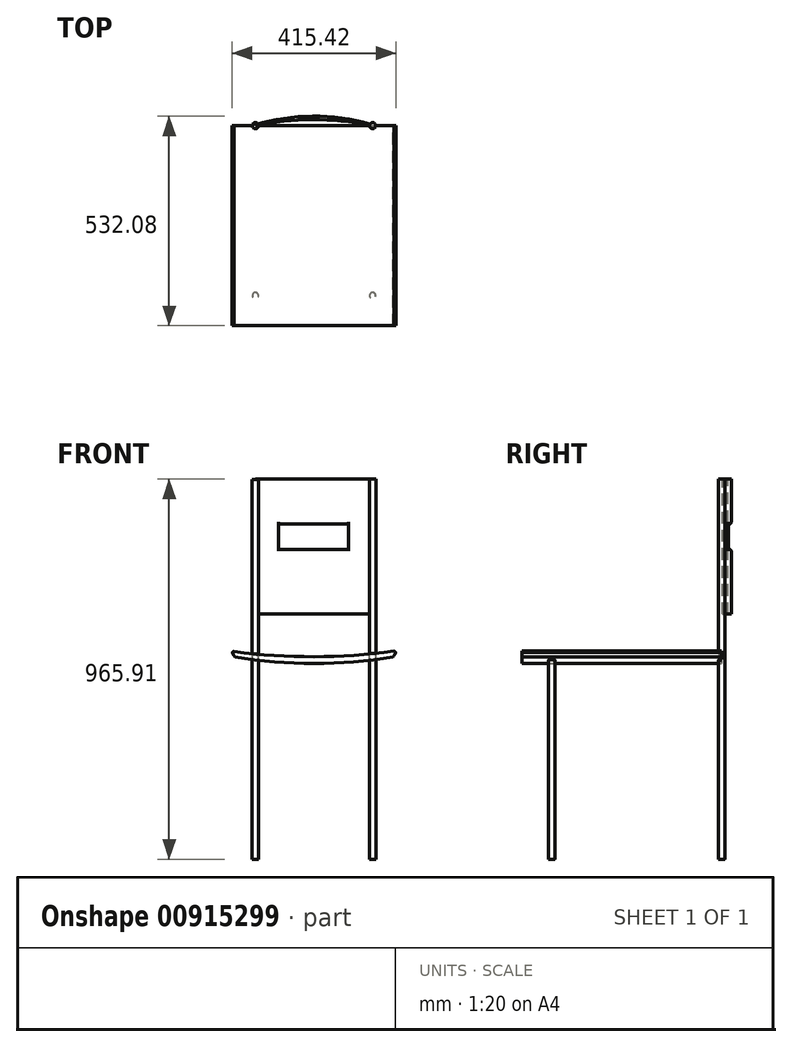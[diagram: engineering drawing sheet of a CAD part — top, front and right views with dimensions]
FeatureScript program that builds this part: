
annotation { "Feature Type Name" : "Feature", "Feature Type Description" : "" }
export const myFeature = defineFeature(function(context is Context, id is Id, definition is map)
    precondition{}
    {
        {
            var Q0;
            Q0=qCreatedBy(makeId("Front.planeOp"),FACE);
            var sketch = newSketch(context, id + "F0", { "sketchPlane" : qUnion([Q0])});
            skArc(sketch, "E0", {"start": v(-203.45, 18.1) * mm, "mid": v(-0.2, 5.21) * mm, "end": v(202.95, 19.47) * mm});
            skArc(sketch, "E1", {"start": v(-203.45, 18.1) * mm, "mid": v(-206.06, 17.6) * mm, "end": v(-207.7, 15.52) * mm});
            skLineSegment(sketch, "E2", {"start": v(-207.7, 15.52) * mm, "end": v(-207.17, 15.52) * mm});
            skArc(sketch, "E3", {"start": v(-207.17, 15.52) * mm, "mid": v(-204.63, 10.07) * mm, "end": v(-201.09, 5.21) * mm});
            skArc(sketch, "E4.MirrorCS", {"start": v(207.17, 15.52) * mm, "mid": v(204.63, 10.07) * mm, "end": v(201.09, 5.21) * mm});
            skLineSegment(sketch, "E5.MirrorCS", {"start": v(207.7, 15.52) * mm, "end": v(207.17, 15.52) * mm});
            skArc(sketch, "E6", {"start": v(207.7, 15.52) * mm, "mid": v(205.84, 18.1) * mm, "end": v(202.95, 19.47) * mm});
            skArc(sketch, "E7", {"start": v(-201.09, 5.21) * mm, "mid": v(0, -12.16) * mm, "end": v(201.09, 5.21) * mm});
            skArc(sketch, "E8", {"start": v(-207.17, 15.52) * mm, "mid": v(0, -0.55) * mm, "end": v(207.17, 15.52) * mm});
            skSolve(sketch);
        }
        {
            var Q0;
            Q0=makeQuery(id+"F0.imprint","IMPRINT",FACE,{"disambiguationData":[TD([[makeQuery(id+"F0.imprint","IMPRINT",EDGE,{"derivedFrom":sQuery(id+"F0.wireOp",EDGE,"E3")}),1.0]])]});
            var Q1;
            Q1=makeQuery(id+"F0.imprint","IMPRINT",FACE,{"disambiguationData":[TD([[makeQuery(id+"F0.imprint","IMPRINT",EDGE,{"derivedFrom":sQuery(id+"F0.wireOp",EDGE,"E0")}),-1.0]])]});
            extrude(context, id + "F1", {"entities" : qUnion([Q0, Q1]), "endBound" : BoundingType.SYMMETRIC, "depth" : 508 * mm, "offsetDistance" : 25.4 * mm});
        }
        {
            var Q0;
            Q0=makeQuery(id+"F1.opExtrude","CAP_FACE",FACE,{"disambiguationData":[OSD([sQuery(id+"F0.wireOp",EDGE,"E0"),sQuery(id+"F0.wireOp",EDGE,"E1"),sQuery(id+"F0.wireOp",EDGE,"E2"),sQuery(id+"F0.wireOp",EDGE,"E3"),sQuery(id+"F0.wireOp",EDGE,"E4.MirrorCS"),sQuery(id+"F0.wireOp",EDGE,"E5.MirrorCS"),sQuery(id+"F0.wireOp",EDGE,"E6"),sQuery(id+"F0.wireOp",EDGE,"E7")])],"isStart":true});
            var sketch = newSketch(context, id + "F2", { "sketchPlane" : qUnion([Q0])});
            skLineSegment(sketch, "E9.MirrorCS", {"start": v(156.85, -1.46) * mm, "end": v(156.85, -509.46) * mm});
            skLineSegment(sketch, "E10", {"start": v(-156.85, -0.75) * mm, "end": v(-156.85, -509.46) * mm});
            skLineSegment(sketch, "E11", {"start": v(-149.06, -2.65) * mm, "end": v(-149.06, -509.46) * mm});
            skLineSegment(sketch, "E12.MirrorCS", {"start": v(149.06, -2.65) * mm, "end": v(149.06, -509.46) * mm});
            skLineSegment(sketch, "E13", {"start": v(-156.85, -509.46) * mm, "end": v(-149.06, -509.46) * mm});
            skLineSegment(sketch, "E14.MirrorCS", {"start": v(156.85, -509.46) * mm, "end": v(149.06, -509.46) * mm});
            skLineSegment(sketch, "E15", {"start": v(-156.85, -0.75) * mm, "end": v(-156.85, 456.45) * mm});
            skLineSegment(sketch, "E16", {"start": v(-149.06, -2.65) * mm, "end": v(-149.06, 456.45) * mm});
            skLineSegment(sketch, "E17", {"start": v(149.06, -2.65) * mm, "end": v(149.06, 454.55) * mm});
            skLineSegment(sketch, "E18", {"start": v(156.85, -1.46) * mm, "end": v(156.85, 455.74) * mm});
            skLineSegment(sketch, "E19", {"start": v(-149.06, 456.45) * mm, "end": v(-156.85, 456.45) * mm});
            skLineSegment(sketch, "E20", {"start": v(156.85, 455.74) * mm, "end": v(149.06, 454.55) * mm});
            skSolve(sketch);
        }
        {
            var Q0;
            {var subQ4=sQuery(id+"F2.wireOp",EDGE,"E11");Q0=makeQuery(id+"F2.imprint","IMPRINT",FACE,{"disambiguationData":[TD([[makeQuery(id+"F2.imprint","IMPRINT",EDGE,{"derivedFrom":subQ4}),-1.0]])]});}
            var Q1;
            Q1=sQuery(id+"F2.wireOp",EDGE,"E11");
            revolve(context, id + "F3", {"operationType" : NewBodyOperationType.ADD, "surfaceOperationType" : NewSurfaceOperationType.NEW, "entities" : qUnion([Q0]), "axis" : qUnion([Q1]), "revolveType" : RevolveType.FULL});
        }
        {
            var Q0;
            {var subQ4=sQuery(id+"F2.wireOp",EDGE,"E12.MirrorCS");Q0=makeQuery(id+"F2.imprint","IMPRINT",FACE,{"disambiguationData":[TD([[makeQuery(id+"F2.imprint","IMPRINT",EDGE,{"derivedFrom":subQ4}),1.0]])]});}
            var Q1;
            Q1=sQuery(id+"F2.wireOp",EDGE,"E12.MirrorCS");
            revolve(context, id + "F4", {"operationType" : NewBodyOperationType.ADD, "surfaceOperationType" : NewSurfaceOperationType.NEW, "entities" : qUnion([Q0]), "axis" : qUnion([Q1]), "revolveType" : RevolveType.FULL});
        }
        {
            var Q0;
            Q0=makeQuery(id+"F1.opExtrude","CAP_FACE",FACE,{"disambiguationData":[OSD([sQuery(id+"F0.wireOp",EDGE,"E0"),sQuery(id+"F0.wireOp",EDGE,"E1"),sQuery(id+"F0.wireOp",EDGE,"E2"),sQuery(id+"F0.wireOp",EDGE,"E3"),sQuery(id+"F0.wireOp",EDGE,"E4.MirrorCS"),sQuery(id+"F0.wireOp",EDGE,"E5.MirrorCS"),sQuery(id+"F0.wireOp",EDGE,"E6"),sQuery(id+"F0.wireOp",EDGE,"E7")])],"isStart":false});
            cPlane(context, id + "F5", {"entities" : qUnion([Q0]), "cplaneType" : CPlaneType.OFFSET, "offset" : 76.2 * mm, "oppositeDirection" : true, "width" : 152.4 * mm, "height" : 152.4 * mm});
        }
        {
            var Q0;
            Q0=qCreatedBy(id+"F5.planeOp",FACE);
            var sketch = newSketch(context, id + "F6", { "sketchPlane" : qUnion([Q0])});
            skLineSegment(sketch, "E21.0", {"start": v(-149.06, -2.65) * mm, "end": v(-149.06, -509.46) * mm});
            skLineSegment(sketch, "E22.0", {"start": v(-156.85, -1.46) * mm, "end": v(-156.85, -509.46) * mm});
            skLineSegment(sketch, "E23.0", {"start": v(149.06, -2.65) * mm, "end": v(149.06, -509.46) * mm});
            skLineSegment(sketch, "E24", {"start": v(156.85, -1.62) * mm, "end": v(156.85, -509.46) * mm});
            skLineSegment(sketch, "E25.0", {"start": v(156.85, -509.46) * mm, "end": v(149.06, -509.46) * mm});
            skLineSegment(sketch, "E26.0", {"start": v(-156.85, -509.46) * mm, "end": v(-149.06, -509.46) * mm});
            skLineSegment(sketch, "E27", {"start": v(-156.85, -1.46) * mm, "end": v(-149.06, -2.65) * mm});
            skLineSegment(sketch, "E28", {"start": v(149.06, -2.65) * mm, "end": v(156.85, -1.62) * mm});
            skSolve(sketch);
        }
        {
            var Q0;
            Q0=makeQuery(id+"F6.imprint","IMPRINT",FACE,{"disambiguationData":[TD([[makeQuery(id+"F6.imprint","IMPRINT",EDGE,{"derivedFrom":sQuery(id+"F6.wireOp",EDGE,"E21.0")}),-1.0]])]});
            var Q1;
            Q1=sQuery(id+"F6.wireOp",EDGE,"E21.0");
            revolve(context, id + "F7", {"operationType" : NewBodyOperationType.ADD, "surfaceOperationType" : NewSurfaceOperationType.NEW, "entities" : qUnion([Q0]), "axis" : qUnion([Q1]), "revolveType" : RevolveType.FULL});
        }
        {
            var Q0;
            Q0=makeQuery(id+"F6.imprint","IMPRINT",FACE,{"disambiguationData":[TD([[makeQuery(id+"F6.imprint","IMPRINT",EDGE,{"derivedFrom":sQuery(id+"F6.wireOp",EDGE,"E23.0")}),1.0]])]});
            var Q1;
            Q1=sQuery(id+"F6.wireOp",EDGE,"E23.0");
            revolve(context, id + "F8", {"operationType" : NewBodyOperationType.ADD, "surfaceOperationType" : NewSurfaceOperationType.NEW, "entities" : qUnion([Q0]), "axis" : qUnion([Q1]), "revolveType" : RevolveType.FULL});
        }
        {
            var Q0;
            {var subQ1=sQuery(id+"F2.wireOp",EDGE,"E16");Q0=makeQuery(id+"F2.imprint","IMPRINT",FACE,{"disambiguationData":[TD([[makeQuery(id+"F2.imprint","IMPRINT",EDGE,{"derivedFrom":subQ1}),1.0]])]});}
            var Q1;
            Q1=sQuery(id+"F2.wireOp",EDGE,"E16");
            revolve(context, id + "F9", {"operationType" : NewBodyOperationType.ADD, "surfaceOperationType" : NewSurfaceOperationType.NEW, "entities" : qUnion([Q0]), "axis" : qUnion([Q1]), "revolveType" : RevolveType.FULL});
        }
        {
            var Q0;
            {var subQ1=sQuery(id+"F2.wireOp",EDGE,"E17");Q0=makeQuery(id+"F2.imprint","IMPRINT",FACE,{"disambiguationData":[TD([[makeQuery(id+"F2.imprint","IMPRINT",EDGE,{"derivedFrom":subQ1}),-1.0]])]});}
            var Q1;
            Q1=sQuery(id+"F2.wireOp",EDGE,"E17");
            revolve(context, id + "F10", {"operationType" : NewBodyOperationType.ADD, "surfaceOperationType" : NewSurfaceOperationType.NEW, "entities" : qUnion([Q0]), "axis" : qUnion([Q1]), "revolveType" : RevolveType.FULL});
        }
        {
            var Q0;
            {var subQ3=sQuery(id+"F2.wireOp",EDGE,"E10");var subQ5=sQuery(id+"F2.wireOp",EDGE,"E15");var subQ6=makeQuery(id+"F2.imprint","INTERSECT",VERTEX,{"derivedFrom":[subQ3,subQ5]});Q0=makeQuery(id+"F2.imprint","IMPRINT",FACE,{"disambiguationData":[TD([[makeQuery(id+"F2.imprint","IMPRINT",EDGE,{"disambiguationData":[TD([[subQ6,-1.0]])],"derivedFrom":subQ3}),1.0]])]});}
            var Q1;
            Q1=sQuery(id+"F2.wireOp",EDGE,"E16");
            revolve(context, id + "F11", {"operationType" : NewBodyOperationType.ADD, "surfaceOperationType" : NewSurfaceOperationType.NEW, "entities" : qUnion([Q0]), "axis" : qUnion([Q1]), "revolveType" : RevolveType.ONE_DIRECTION, "angle" : 180 * degree});
        }
        {
            var Q0;
            {var subQ3=sQuery(id+"F2.wireOp",EDGE,"E9.MirrorCS");var subQ5=sQuery(id+"F2.wireOp",EDGE,"E18");var subQ6=makeQuery(id+"F2.imprint","INTERSECT",VERTEX,{"derivedFrom":[subQ3,subQ5]});Q0=makeQuery(id+"F2.imprint","IMPRINT",FACE,{"disambiguationData":[TD([[makeQuery(id+"F2.imprint","IMPRINT",EDGE,{"disambiguationData":[TD([[subQ6,-1.0]])],"derivedFrom":subQ3}),-1.0]])]});}
            var Q1;
            Q1=sQuery(id+"F2.wireOp",EDGE,"E17");
            revolve(context, id + "F12", {"operationType" : NewBodyOperationType.ADD, "surfaceOperationType" : NewSurfaceOperationType.NEW, "entities" : qUnion([Q0]), "axis" : qUnion([Q1]), "revolveType" : RevolveType.ONE_DIRECTION, "angle" : 0 * degree});
        }
        {
            var Q0;
            Q0=makeQuery(id+"F9.opRevolve","SWEPT_FACE",FACE,{"disambiguationData":[OSD([sQuery(id+"F2.wireOp",EDGE,"E19")])]});
            var sketch = newSketch(context, id + "F13", { "sketchPlane" : qUnion([Q0])});
            skArc(sketch, "E29", {"start": v(149.06, 254) * mm, "mid": v(0, 269.39) * mm, "end": v(-149.06, 254) * mm});
            skLineSegment(sketch, "E30", {"start": v(-149.06, 254) * mm, "end": v(-149.06, 256.54) * mm});
            skLineSegment(sketch, "E31", {"start": v(149.06, 254) * mm, "end": v(149.06, 256.54) * mm});
            skArc(sketch, "E32", {"start": v(149.06, 256.54) * mm, "mid": v(0, 278.08) * mm, "end": v(-149.06, 256.54) * mm});
            skSolve(sketch);
        }
        {
            var Q0;
            {var subQ0=sQuery(id+"F13.wireOp",EDGE,"E30");Q0=makeQuery(id+"F13.imprint","IMPRINT",FACE,{"disambiguationData":[TD([[makeQuery(id+"F13.imprint","IMPRINT",EDGE,{"derivedFrom":subQ0}),-1.0]])]});}
            extrude(context, id + "F14", {"entities" : qUnion([Q0]), "operationType" : NewBodyOperationType.ADD, "oppositeDirection" : true, "depth" : 342.9 * mm, "offsetDistance" : 25.4 * mm});
        }
        {
            var Q0;
            Q0=qCreatedBy(makeId("Front.planeOp"),FACE);
            var sketch = newSketch(context, id + "F15", { "sketchPlane" : qUnion([Q0])});
            skLineSegment(sketch, "E33.bottom", {"start": v(-90.61, 278.39) * mm, "end": v(87.19, 278.39) * mm});
            skLineSegment(sketch, "E33.top", {"start": v(-90.61, 341.89) * mm, "end": v(87.19, 341.89) * mm});
            skLineSegment(sketch, "E33.left", {"start": v(-90.61, 278.39) * mm, "end": v(-90.61, 341.89) * mm});
            skLineSegment(sketch, "E33.right", {"start": v(87.19, 278.39) * mm, "end": v(87.19, 341.89) * mm});
            skSolve(sketch);
        }
        {
            var Q0;
            Q0=makeQuery(id+"F15.imprint","IMPRINT",FACE,{"disambiguationData":[TD([[makeQuery(id+"F15.imprint","IMPRINT",EDGE,{"derivedFrom":sQuery(id+"F15.wireOp",EDGE,"E33.bottom")}),1.0]])]});
            extrude(context, id + "F16", {"entities" : qUnion([Q0]), "operationType" : NewBodyOperationType.REMOVE, "endBound" : BoundingType.THROUGH_ALL, "oppositeDirection" : true, "depth" : 25.4 * mm, "offsetDistance" : 25.4 * mm});
        }
        {
            var Q0;
            Q0=makeQuery(id+"F16.boolean.opBoolean","INTERSECT",EDGE,{"derivedFrom":[makeQuery(id+"F14.opExtrude","SWEPT_FACE",FACE,{"disambiguationData":[OSD([sQuery(id+"F13.wireOp",EDGE,"E32")])]}),makeQuery(id+"F16.opExtrude","SWEPT_FACE",FACE,{"disambiguationData":[OSD([sQuery(id+"F15.wireOp",EDGE,"E33.bottom")])]})]});
            var Q1;
            Q1=makeQuery(id+"F16.boolean.opBoolean","INTERSECT",EDGE,{"derivedFrom":[makeQuery(id+"F14.opExtrude","SWEPT_FACE",FACE,{"disambiguationData":[OSD([sQuery(id+"F13.wireOp",EDGE,"E29")])]}),makeQuery(id+"F16.opExtrude","SWEPT_FACE",FACE,{"disambiguationData":[OSD([sQuery(id+"F15.wireOp",EDGE,"E33.bottom")])]})]});
            var Q2;
            Q2=makeQuery(id+"F16.boolean.opBoolean","INTERSECT",EDGE,{"derivedFrom":[makeQuery(id+"F14.opExtrude","SWEPT_FACE",FACE,{"disambiguationData":[OSD([sQuery(id+"F13.wireOp",EDGE,"E32")])]}),makeQuery(id+"F16.opExtrude","SWEPT_FACE",FACE,{"disambiguationData":[OSD([sQuery(id+"F15.wireOp",EDGE,"E33.top")])]})]});
            var Q3;
            Q3=makeQuery(id+"F16.boolean.opBoolean","INTERSECT",EDGE,{"derivedFrom":[makeQuery(id+"F14.opExtrude","SWEPT_FACE",FACE,{"disambiguationData":[OSD([sQuery(id+"F13.wireOp",EDGE,"E29")])]}),makeQuery(id+"F16.opExtrude","SWEPT_FACE",FACE,{"disambiguationData":[OSD([sQuery(id+"F15.wireOp",EDGE,"E33.top")])]})]});
            fillet(context, id + "F17", {"entities" : qUnion([Q0, Q1, Q2, Q3]), "radius" : 5.08 * mm, "tangentPropagation" : true, "allowEdgeOverflow" : false});
        }
    });
